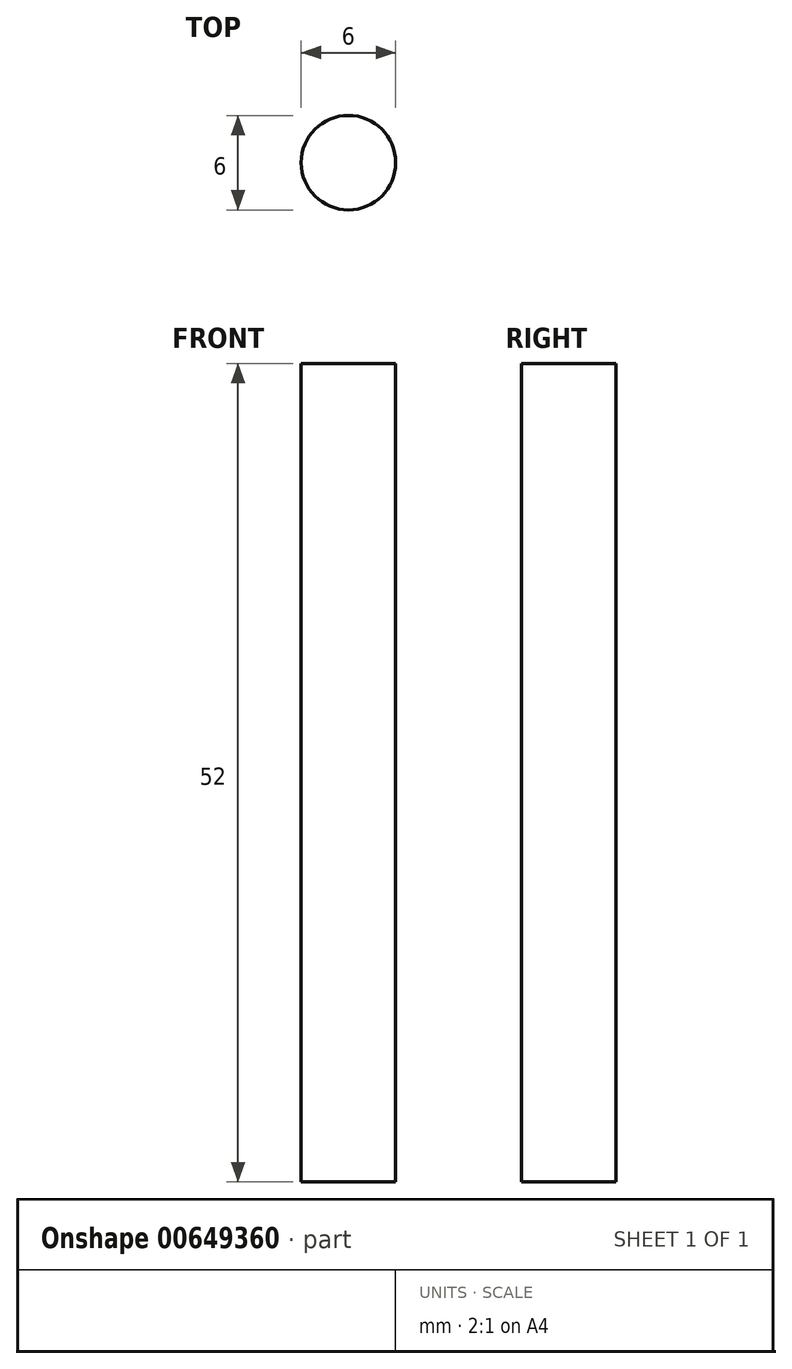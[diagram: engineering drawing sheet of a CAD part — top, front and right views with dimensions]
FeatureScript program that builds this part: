
annotation { "Feature Type Name" : "Feature", "Feature Type Description" : "" }
export const myFeature = defineFeature(function(context is Context, id is Id, definition is map)
    precondition{}
    {
        {
            var Q0;
            Q0=qCreatedBy(makeId("Top.planeOp"),FACE);
            var sketch = newSketch(context, id + "F0", { "sketchPlane" : qUnion([Q0])});
            skCircle(sketch, "E0", {"center": v(0, 0) * mm, "radius": 3 * mm});
            skSolve(sketch);
        }
        {
            var Q0;
            Q0 = qSketchRegion(id + "F0", true);
            extrude(context, id + "F1", {"entities" : qUnion([Q0]), "depth" : 52 * mm, "offsetDistance" : 25 * mm});
        }
    });
